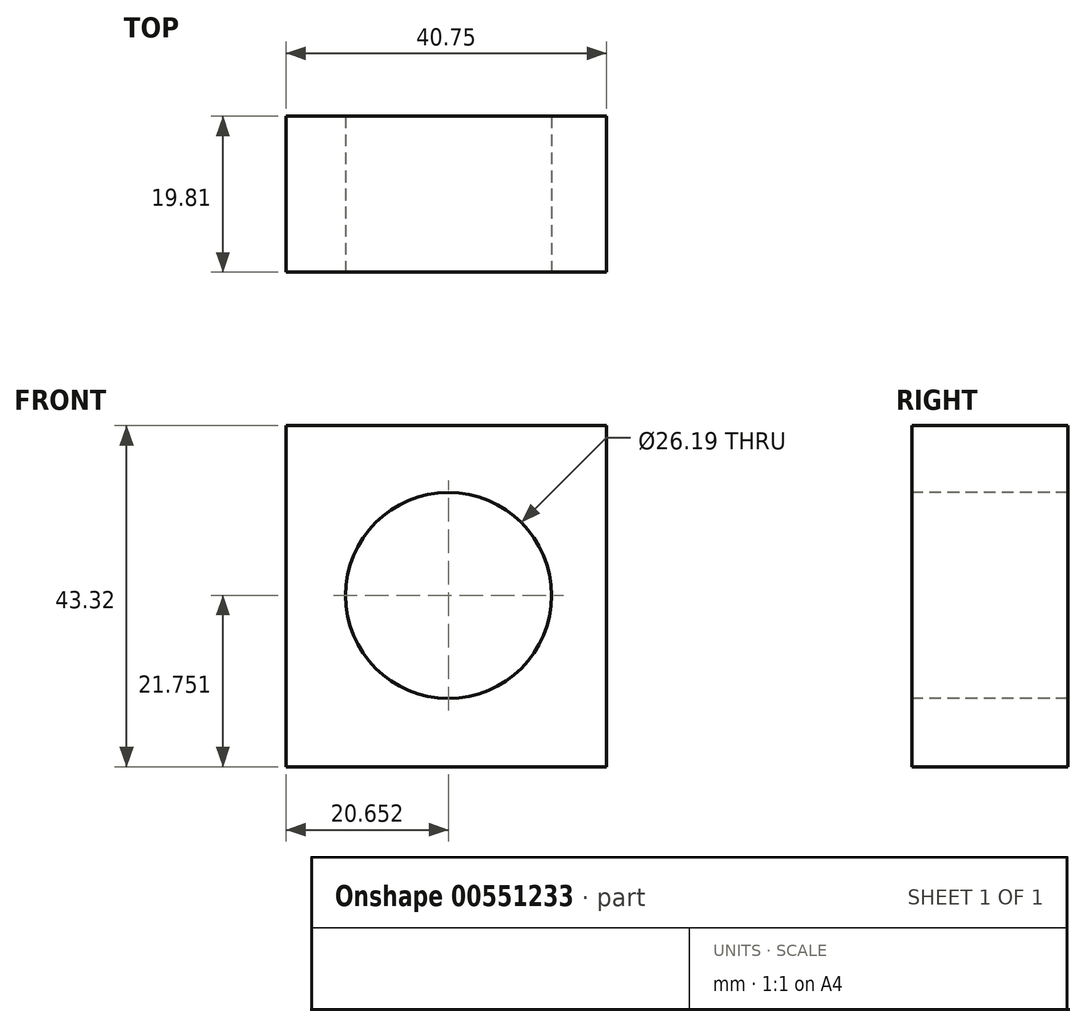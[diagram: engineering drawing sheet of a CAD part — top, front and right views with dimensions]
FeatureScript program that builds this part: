
annotation { "Feature Type Name" : "Feature", "Feature Type Description" : "" }
export const myFeature = defineFeature(function(context is Context, id is Id, definition is map)
    precondition{}
    {
        {
            var Q0;
            Q0=qCreatedBy(makeId("Front.planeOp"),FACE);
            var sketch = newSketch(context, id + "F0", { "sketchPlane" : qUnion([Q0])});
            skLineSegment(sketch, "E0.bottom", {"start": v(-59.92, 32.63) * mm, "end": v(-19.17, 32.63) * mm});
            skLineSegment(sketch, "E0.top", {"start": v(-59.92, -10.7) * mm, "end": v(-19.17, -10.7) * mm});
            skLineSegment(sketch, "E0.left", {"start": v(-59.92, 32.63) * mm, "end": v(-59.92, -10.7) * mm});
            skLineSegment(sketch, "E0.right", {"start": v(-19.17, 32.63) * mm, "end": v(-19.17, -10.7) * mm});
            skSolve(sketch);
        }
        {
            var Q0;
            Q0=makeQuery(id+"F0.imprint","IMPRINT",FACE,{"disambiguationData":[TD([[makeQuery(id+"F0.imprint","IMPRINT",EDGE,{"derivedFrom":sQuery(id+"F0.wireOp",EDGE,"E0.bottom")}),-1.0]])]});
            extrude(context, id + "F1", {"entities" : qUnion([Q0]), "depth" : 19.8 * mm, "offsetDistance" : 25.4 * mm});
        }
        {
            var Q0;
            Q0=makeQuery(id+"F1.opExtrude","CAP_FACE",FACE,{"disambiguationData":[OSD([sQuery(id+"F0.wireOp",EDGE,"E0.bottom"),sQuery(id+"F0.wireOp",EDGE,"E0.top"),sQuery(id+"F0.wireOp",EDGE,"E0.left"),sQuery(id+"F0.wireOp",EDGE,"E0.right")])],"isStart":false});
            var sketch = newSketch(context, id + "F2", { "sketchPlane" : qUnion([Q0])});
            skCircle(sketch, "E1", {"center": v(-39.27, 11.06) * mm, "radius": 13.1 * mm});
            skSolve(sketch);
        }
        {
            var Q0;
            Q0=makeQuery(id+"F2.imprint","IMPRINT",FACE,{"disambiguationData":[TD([[makeQuery(id+"F2.imprint","IMPRINT",EDGE,{"derivedFrom":sQuery(id+"F2.wireOp",EDGE,"E1")}),1.0]])]});
            extrude(context, id + "F3", {"entities" : qUnion([Q0]), "operationType" : NewBodyOperationType.REMOVE, "oppositeDirection" : true, "depth" : 26.92 * mm, "offsetDistance" : 25.4 * mm});
        }
    });
